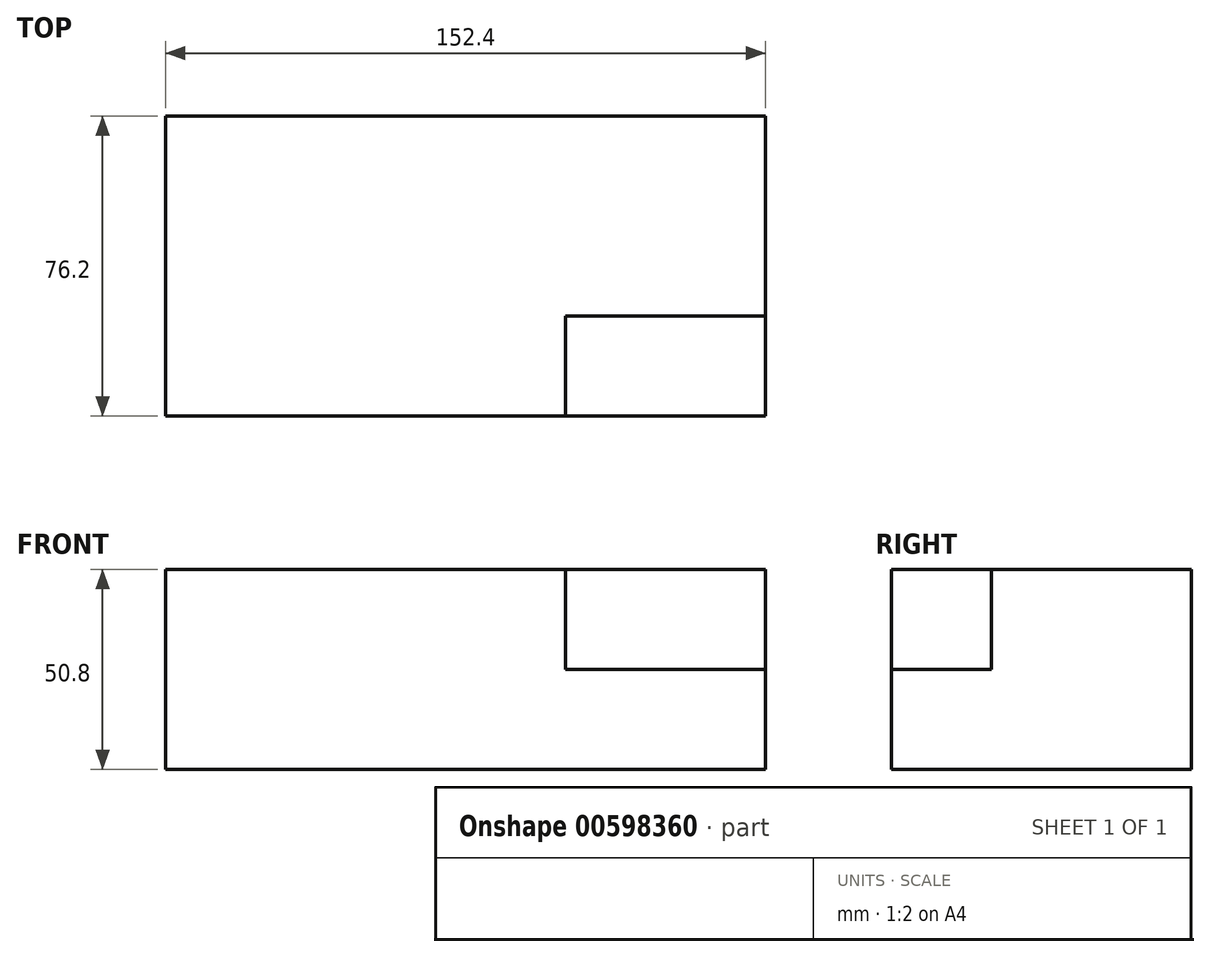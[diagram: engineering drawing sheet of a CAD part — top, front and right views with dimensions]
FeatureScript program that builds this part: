
annotation { "Feature Type Name" : "Feature", "Feature Type Description" : "" }
export const myFeature = defineFeature(function(context is Context, id is Id, definition is map)
    precondition{}
    {
        {
            var Q0;
            Q0=qCreatedBy(makeId("Front.planeOp"),FACE);
            var sketch = newSketch(context, id + "F0", { "sketchPlane" : qUnion([Q0])});
            skLineSegment(sketch, "E0", {"start": v(0, 25.4) * mm, "end": v(0, 0) * mm});
            skLineSegment(sketch, "E1", {"start": v(0, 0) * mm, "end": v(-152.4, 0) * mm});
            skLineSegment(sketch, "E2", {"start": v(-152.4, 0) * mm, "end": v(-152.4, 50.8) * mm});
            skLineSegment(sketch, "E3", {"start": v(-152.4, 50.8) * mm, "end": v(-50.8, 50.8) * mm});
            skLineSegment(sketch, "E4", {"start": v(-50.8, 50.8) * mm, "end": v(-50.8, 25.4) * mm});
            skLineSegment(sketch, "E5", {"start": v(-50.8, 25.4) * mm, "end": v(0, 25.4) * mm});
            skSolve(sketch);
        }
        {
            var Q0;
            Q0=makeQuery(id+"F0.imprint","IMPRINT",FACE,{"disambiguationData":[TD([[makeQuery(id+"F0.imprint","IMPRINT",EDGE,{"derivedFrom":sQuery(id+"F0.wireOp",EDGE,"E0")}),-1.0]])]});
            extrude(context, id + "F1", {"entities" : qUnion([Q0]), "depth" : 76.2 * mm, "offsetDistance" : 25.4 * mm});
        }
        {
            var Q0;
            Q0=makeQuery(id+"F1.opExtrude","SWEPT_FACE",FACE,{"disambiguationData":[OSD([sQuery(id+"F0.wireOp",EDGE,"E4")])]});
            var sketch = newSketch(context, id + "F2", { "sketchPlane" : qUnion([Q0])});
            skLineSegment(sketch, "E6", {"start": v(0, 50.8) * mm, "end": v(-50.8, 50.8) * mm});
            skLineSegment(sketch, "E7", {"start": v(-50.8, 50.8) * mm, "end": v(-50.8, 25.4) * mm});
            skSolve(sketch);
        }
        {
            var Q0;
            Q0=makeQuery(id+"F2.imprint","IMPRINT",FACE,{"disambiguationData":[TD([[makeQuery(id+"F2.imprint","IMPRINT",EDGE,{"derivedFrom":sQuery(id+"F2.wireOp",EDGE,"E6")}),-1.0]])]});
            extrude(context, id + "F3", {"entities" : qUnion([Q0]), "operationType" : NewBodyOperationType.ADD, "depth" : 50.8 * mm, "offsetDistance" : 25.4 * mm});
        }
    });
